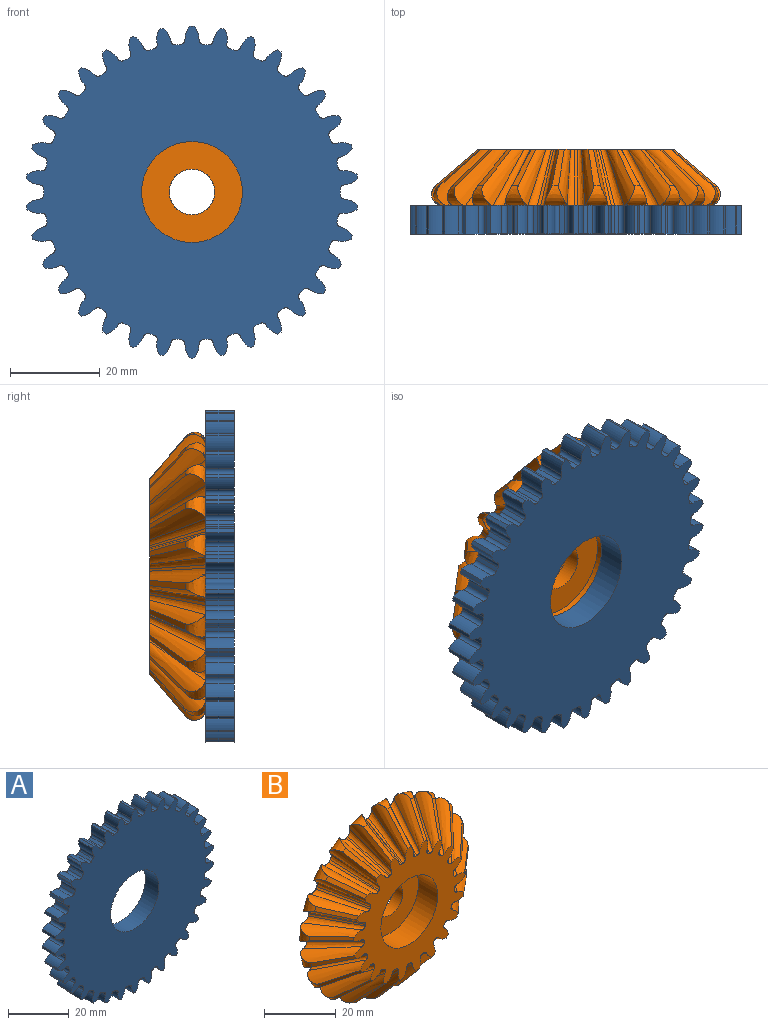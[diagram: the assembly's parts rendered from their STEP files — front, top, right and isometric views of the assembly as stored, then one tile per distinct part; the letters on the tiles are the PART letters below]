
ASSEMBLY  parts=2 mates=1
PART A: 207 faces, bbox 73.8x6.4x74 mm
  f0: cylinder r=33mm len=6.35mm, axis (0,1,0), area 7mm2, adj f34,f35,f40,f204
  f1: cylinder r=33mm len=6.35mm, axis (0,1,0), area 7mm2, adj f34,f35,f199,f205
  f2: cylinder r=33mm len=6.35mm, axis (0,1,0), area 7mm2, adj f34,f35,f194,f200
  f3: cylinder r=33mm len=6.35mm, axis (0,1,0), area 7mm2, adj f34,f35,f189,f195
  f4: cylinder r=33mm len=6.35mm, axis (0,1,0), area 7mm2, adj f34,f35,f184,f190
  f5: cylinder r=33mm len=6.35mm, axis (0,1,0), area 7mm2, adj f34,f35,f179,f185
  f6: cylinder r=33mm len=6.35mm, axis (0,1,0), area 7mm2, adj f34,f35,f174,f180
  f7: cylinder r=33mm len=6.35mm, axis (0,1,0), area 7mm2, adj f34,f35,f169,f175
  f8: cylinder r=33mm len=6.35mm, axis (0,1,0), area 7mm2, adj f34,f35,f164,f170
  f9: cylinder r=33mm len=6.35mm, axis (0,1,0), area 7mm2, adj f34,f35,f159,f165
  f10: cylinder r=33mm len=6.35mm, axis (0,1,0), area 7mm2, adj f34,f35,f154,f160
  f11: cylinder r=33mm len=6.35mm, axis (0,1,0), area 7mm2, adj f34,f35,f149,f155
  f12: cylinder r=33mm len=6.35mm, axis (0,1,0), area 7mm2, adj f34,f35,f144,f150
  f13: cylinder r=33mm len=6.35mm, axis (0,1,0), area 7mm2, adj f34,f35,f139,f145
  f14: cylinder r=33mm len=6.35mm, axis (0,1,0), area 7mm2, adj f34,f35,f134,f140
  f15: cylinder r=33mm len=6.35mm, axis (0,1,0), area 7mm2, adj f34,f35,f129,f135
  f16: cylinder r=33mm len=6.35mm, axis (0,1,0), area 7mm2, adj f34,f35,f124,f130
  f17: cylinder r=33mm len=6.35mm, axis (0,1,0), area 7mm2, adj f34,f35,f119,f125
  f18: cylinder r=33mm len=6.35mm, axis (0,1,0), area 7mm2, adj f34,f35,f114,f120
  f19: cylinder r=33mm len=6.35mm, axis (0,1,0), area 7mm2, adj f34,f35,f109,f115
  f20: cylinder r=33mm len=6.35mm, axis (0,1,0), area 7mm2, adj f34,f35,f104,f110
  f21: cylinder r=33mm len=6.35mm, axis (0,1,0), area 7mm2, adj f34,f35,f99,f105
  f22: cylinder r=33mm len=6.35mm, axis (0,1,0), area 7mm2, adj f34,f35,f94,f100
  f23: cylinder r=33mm len=6.35mm, axis (0,1,0), area 7mm2, adj f34,f35,f89,f95
  f24: cylinder r=33mm len=6.35mm, axis (0,1,0), area 7mm2, adj f34,f35,f84,f90
  f25: cylinder r=33mm len=6.35mm, axis (0,1,0), area 7mm2, adj f34,f35,f79,f85
  f26: cylinder r=33mm len=6.35mm, axis (0,1,0), area 7mm2, adj f34,f35,f74,f80
  f27: cylinder r=33mm len=6.35mm, axis (0,1,0), area 7mm2, adj f34,f35,f69,f75
  f28: cylinder r=33mm len=6.35mm, axis (0,1,0), area 7mm2, adj f34,f35,f64,f70
  f29: cylinder r=33mm len=6.35mm, axis (0,1,0), area 7mm2, adj f34,f35,f59,f65
  f30: cylinder r=33mm len=6.35mm, axis (0,1,0), area 7mm2, adj f34,f35,f54,f60
  f31: cylinder r=33mm len=6.35mm, axis (0,1,0), area 7mm2, adj f34,f35,f49,f55
  f32: cylinder r=33mm len=6.35mm, axis (0,1,0), area 7mm2, adj f34,f35,f44,f50
  f33: cylinder r=33mm len=6.35mm, axis (0,1,0), area 7mm2, adj f34,f35,f39,f45
  f34: plane 74x73.76mm, normal (0,-1,0), area 3393.5mm2, adj f0,f1,f2,f3,f4,f5,f6,f7
  f35: plane 74x73.76mm, normal (0,1,0), area 3393.5mm2, adj f0,f1,f2,f3,f4,f5,f6,f7
  f36: cylinder r=4.53mm len=6.35mm, axis (0,1,0), area 21.2mm2, adj f34,f35,f37,f40
  f37: cylinder r=37mm len=6.35mm, axis (0,1,0), area 5.8mm2, adj f34,f35,f36,f38
  f38: cylinder r=4.53mm len=6.35mm, axis (0,1,0), area 21.2mm2, adj f34,f35,f37,f39
  f39: cylinder r=1mm len=6.35mm, axis (0,1,0), area 9.6mm2, adj f33,f34,f35,f38
  f40: cylinder r=1mm len=6.35mm, axis (0,1,0), area 9.6mm2, adj f0,f34,f35,f36
  f41: cylinder r=4.53mm len=6.35mm, axis (0,1,0), area 21.2mm2, adj f34,f35,f42,f45
  f42: cylinder r=37mm len=6.35mm, axis (0,1,0), area 5.8mm2, adj f34,f35,f41,f43
  f43: cylinder r=4.53mm len=6.35mm, axis (0,1,0), area 21.2mm2, adj f34,f35,f42,f44
  f44: cylinder r=1mm len=6.35mm, axis (0,1,0), area 9.6mm2, adj f32,f34,f35,f43
  f45: cylinder r=1mm len=6.35mm, axis (0,1,0), area 9.6mm2, adj f33,f34,f35,f41
  f46: cylinder r=4.53mm len=6.35mm, axis (0,1,0), area 21.2mm2, adj f34,f35,f47,f50
  f47: cylinder r=37mm len=6.35mm, axis (0,1,0), area 5.8mm2, adj f34,f35,f46,f48
  f48: cylinder r=4.53mm len=6.35mm, axis (0,1,0), area 21.2mm2, adj f34,f35,f47,f49
  f49: cylinder r=1mm len=6.35mm, axis (0,1,0), area 9.6mm2, adj f31,f34,f35,f48
  f50: cylinder r=1mm len=6.35mm, axis (0,1,0), area 9.6mm2, adj f32,f34,f35,f46
  f51: cylinder r=4.53mm len=6.35mm, axis (0,1,0), area 21.2mm2, adj f34,f35,f52,f55
  f52: cylinder r=37mm len=6.35mm, axis (0,1,0), area 5.8mm2, adj f34,f35,f51,f53
  f53: cylinder r=4.53mm len=6.35mm, axis (0,1,0), area 21.2mm2, adj f34,f35,f52,f54
  f54: cylinder r=1mm len=6.35mm, axis (0,1,0), area 9.6mm2, adj f30,f34,f35,f53
  f55: cylinder r=1mm len=6.35mm, axis (0,1,0), area 9.6mm2, adj f31,f34,f35,f51
  f56: cylinder r=4.53mm len=6.35mm, axis (0,1,0), area 21.2mm2, adj f34,f35,f57,f60
  f57: cylinder r=37mm len=6.35mm, axis (0,1,0), area 5.8mm2, adj f34,f35,f56,f58
  f58: cylinder r=4.53mm len=6.35mm, axis (0,1,0), area 21.2mm2, adj f34,f35,f57,f59
  f59: cylinder r=1mm len=6.35mm, axis (0,1,0), area 9.6mm2, adj f29,f34,f35,f58
  f60: cylinder r=1mm len=6.35mm, axis (0,1,0), area 9.6mm2, adj f30,f34,f35,f56
  f61: cylinder r=4.53mm len=6.35mm, axis (0,1,0), area 21.2mm2, adj f34,f35,f62,f65
  f62: cylinder r=37mm len=6.35mm, axis (0,1,0), area 5.8mm2, adj f34,f35,f61,f63
  f63: cylinder r=4.53mm len=6.35mm, axis (0,1,0), area 21.2mm2, adj f34,f35,f62,f64
  f64: cylinder r=1mm len=6.35mm, axis (0,1,0), area 9.6mm2, adj f28,f34,f35,f63
  f65: cylinder r=1mm len=6.35mm, axis (0,1,0), area 9.6mm2, adj f29,f34,f35,f61
  f66: cylinder r=4.53mm len=6.35mm, axis (0,1,0), area 21.2mm2, adj f34,f35,f67,f70
  f67: cylinder r=37mm len=6.35mm, axis (0,1,0), area 5.8mm2, adj f34,f35,f66,f68
  f68: cylinder r=4.53mm len=6.35mm, axis (0,1,0), area 21.2mm2, adj f34,f35,f67,f69
  f69: cylinder r=1mm len=6.35mm, axis (0,1,0), area 9.6mm2, adj f27,f34,f35,f68
  f70: cylinder r=1mm len=6.35mm, axis (0,1,0), area 9.6mm2, adj f28,f34,f35,f66
  f71: cylinder r=4.53mm len=6.35mm, axis (0,1,0), area 21.2mm2, adj f34,f35,f72,f75
  f72: cylinder r=37mm len=6.35mm, axis (0,1,0), area 5.8mm2, adj f34,f35,f71,f73
  f73: cylinder r=4.53mm len=6.35mm, axis (0,1,0), area 21.2mm2, adj f34,f35,f72,f74
  f74: cylinder r=1mm len=6.35mm, axis (0,1,0), area 9.6mm2, adj f26,f34,f35,f73
  f75: cylinder r=1mm len=6.35mm, axis (0,1,0), area 9.6mm2, adj f27,f34,f35,f71
  f76: cylinder r=4.53mm len=6.35mm, axis (0,1,0), area 21.2mm2, adj f34,f35,f77,f80
  f77: cylinder r=37mm len=6.35mm, axis (0,1,0), area 5.8mm2, adj f34,f35,f76,f78
  f78: cylinder r=4.53mm len=6.35mm, axis (0,1,0), area 21.2mm2, adj f34,f35,f77,f79
  f79: cylinder r=1mm len=6.35mm, axis (0,1,0), area 9.6mm2, adj f25,f34,f35,f78
  f80: cylinder r=1mm len=6.35mm, axis (0,1,0), area 9.6mm2, adj f26,f34,f35,f76
  f81: cylinder r=4.53mm len=6.35mm, axis (0,1,0), area 21.2mm2, adj f34,f35,f82,f85
  f82: cylinder r=37mm len=6.35mm, axis (0,1,0), area 5.8mm2, adj f34,f35,f81,f83
  f83: cylinder r=4.53mm len=6.35mm, axis (0,1,0), area 21.2mm2, adj f34,f35,f82,f84
  f84: cylinder r=1mm len=6.35mm, axis (0,1,0), area 9.6mm2, adj f24,f34,f35,f83
  f85: cylinder r=1mm len=6.35mm, axis (0,1,0), area 9.6mm2, adj f25,f34,f35,f81
  f86: cylinder r=4.53mm len=6.35mm, axis (0,1,0), area 21.2mm2, adj f34,f35,f87,f90
  f87: cylinder r=37mm len=6.35mm, axis (0,1,0), area 5.8mm2, adj f34,f35,f86,f88
  f88: cylinder r=4.53mm len=6.35mm, axis (0,1,0), area 21.2mm2, adj f34,f35,f87,f89
  f89: cylinder r=1mm len=6.35mm, axis (0,1,0), area 9.6mm2, adj f23,f34,f35,f88
  f90: cylinder r=1mm len=6.35mm, axis (0,1,0), area 9.6mm2, adj f24,f34,f35,f86
  f91: cylinder r=4.53mm len=6.35mm, axis (0,1,0), area 21.2mm2, adj f34,f35,f92,f95
  f92: cylinder r=37mm len=6.35mm, axis (0,1,0), area 5.8mm2, adj f34,f35,f91,f93
  f93: cylinder r=4.53mm len=6.35mm, axis (0,1,0), area 21.2mm2, adj f34,f35,f92,f94
  f94: cylinder r=1mm len=6.35mm, axis (0,1,0), area 9.6mm2, adj f22,f34,f35,f93
  f95: cylinder r=1mm len=6.35mm, axis (0,1,0), area 9.6mm2, adj f23,f34,f35,f91
  f96: cylinder r=4.53mm len=6.35mm, axis (0,1,0), area 21.2mm2, adj f34,f35,f97,f100
  f97: cylinder r=37mm len=6.35mm, axis (0,1,0), area 5.8mm2, adj f34,f35,f96,f98
  f98: cylinder r=4.53mm len=6.35mm, axis (0,1,0), area 21.2mm2, adj f34,f35,f97,f99
  f99: cylinder r=1mm len=6.35mm, axis (0,1,0), area 9.6mm2, adj f21,f34,f35,f98
  f100: cylinder r=1mm len=6.35mm, axis (0,1,0), area 9.6mm2, adj f22,f34,f35,f96
  f101: cylinder r=4.53mm len=6.35mm, axis (0,1,0), area 21.2mm2, adj f34,f35,f102,f105
  f102: cylinder r=37mm len=6.35mm, axis (0,1,0), area 5.8mm2, adj f34,f35,f101,f103
  f103: cylinder r=4.53mm len=6.35mm, axis (0,1,0), area 21.2mm2, adj f34,f35,f102,f104
  f104: cylinder r=1mm len=6.35mm, axis (0,1,0), area 9.6mm2, adj f20,f34,f35,f103
  f105: cylinder r=1mm len=6.35mm, axis (0,1,0), area 9.6mm2, adj f21,f34,f35,f101
  f106: cylinder r=4.53mm len=6.35mm, axis (0,1,0), area 21.2mm2, adj f34,f35,f107,f110
  f107: cylinder r=37mm len=6.35mm, axis (0,1,0), area 5.8mm2, adj f34,f35,f106,f108
  f108: cylinder r=4.53mm len=6.35mm, axis (0,1,0), area 21.2mm2, adj f34,f35,f107,f109
  f109: cylinder r=1mm len=6.35mm, axis (0,1,0), area 9.6mm2, adj f19,f34,f35,f108
  f110: cylinder r=1mm len=6.35mm, axis (0,1,0), area 9.6mm2, adj f20,f34,f35,f106
  f111: cylinder r=4.53mm len=6.35mm, axis (0,1,0), area 21.2mm2, adj f34,f35,f112,f115
  f112: cylinder r=37mm len=6.35mm, axis (0,1,0), area 5.8mm2, adj f34,f35,f111,f113
  f113: cylinder r=4.53mm len=6.35mm, axis (0,1,0), area 21.2mm2, adj f34,f35,f112,f114
  f114: cylinder r=1mm len=6.35mm, axis (0,1,0), area 9.6mm2, adj f18,f34,f35,f113
  f115: cylinder r=1mm len=6.35mm, axis (0,1,0), area 9.6mm2, adj f19,f34,f35,f111
  f116: cylinder r=4.53mm len=6.35mm, axis (0,1,0), area 21.2mm2, adj f34,f35,f117,f120
  f117: cylinder r=37mm len=6.35mm, axis (0,1,0), area 5.8mm2, adj f34,f35,f116,f118
  f118: cylinder r=4.53mm len=6.35mm, axis (0,1,0), area 21.2mm2, adj f34,f35,f117,f119
  f119: cylinder r=1mm len=6.35mm, axis (0,1,0), area 9.6mm2, adj f17,f34,f35,f118
  f120: cylinder r=1mm len=6.35mm, axis (0,1,0), area 9.6mm2, adj f18,f34,f35,f116
  f121: cylinder r=4.53mm len=6.35mm, axis (0,1,0), area 21.2mm2, adj f34,f35,f122,f125
  f122: cylinder r=37mm len=6.35mm, axis (0,1,0), area 5.8mm2, adj f34,f35,f121,f123
  f123: cylinder r=4.53mm len=6.35mm, axis (0,1,0), area 21.2mm2, adj f34,f35,f122,f124
  f124: cylinder r=1mm len=6.35mm, axis (0,1,0), area 9.6mm2, adj f16,f34,f35,f123
  f125: cylinder r=1mm len=6.35mm, axis (0,1,0), area 9.6mm2, adj f17,f34,f35,f121
  f126: cylinder r=4.53mm len=6.35mm, axis (0,1,0), area 21.2mm2, adj f34,f35,f127,f130
  f127: cylinder r=37mm len=6.35mm, axis (0,1,0), area 5.8mm2, adj f34,f35,f126,f128
  f128: cylinder r=4.53mm len=6.35mm, axis (0,1,0), area 21.2mm2, adj f34,f35,f127,f129
  f129: cylinder r=1mm len=6.35mm, axis (0,1,0), area 9.6mm2, adj f15,f34,f35,f128
  f130: cylinder r=1mm len=6.35mm, axis (0,1,0), area 9.6mm2, adj f16,f34,f35,f126
  f131: cylinder r=4.53mm len=6.35mm, axis (0,1,0), area 21.2mm2, adj f34,f35,f132,f135
  f132: cylinder r=37mm len=6.35mm, axis (0,1,0), area 5.8mm2, adj f34,f35,f131,f133
  f133: cylinder r=4.53mm len=6.35mm, axis (0,1,0), area 21.2mm2, adj f34,f35,f132,f134
  f134: cylinder r=1mm len=6.35mm, axis (0,1,0), area 9.6mm2, adj f14,f34,f35,f133
  f135: cylinder r=1mm len=6.35mm, axis (0,1,0), area 9.6mm2, adj f15,f34,f35,f131
  f136: cylinder r=4.53mm len=6.35mm, axis (0,1,0), area 21.2mm2, adj f34,f35,f137,f140
  f137: cylinder r=37mm len=6.35mm, axis (0,1,0), area 5.8mm2, adj f34,f35,f136,f138
  f138: cylinder r=4.53mm len=6.35mm, axis (0,1,0), area 21.2mm2, adj f34,f35,f137,f139
  f139: cylinder r=1mm len=6.35mm, axis (0,1,0), area 9.6mm2, adj f13,f34,f35,f138
  f140: cylinder r=1mm len=6.35mm, axis (0,1,0), area 9.6mm2, adj f14,f34,f35,f136
  f141: cylinder r=4.53mm len=6.35mm, axis (0,1,0), area 21.2mm2, adj f34,f35,f142,f145
  f142: cylinder r=37mm len=6.35mm, axis (0,1,0), area 5.8mm2, adj f34,f35,f141,f143
  f143: cylinder r=4.53mm len=6.35mm, axis (0,1,0), area 21.2mm2, adj f34,f35,f142,f144
  f144: cylinder r=1mm len=6.35mm, axis (0,1,0), area 9.6mm2, adj f12,f34,f35,f143
  f145: cylinder r=1mm len=6.35mm, axis (0,1,0), area 9.6mm2, adj f13,f34,f35,f141
  f146: cylinder r=4.53mm len=6.35mm, axis (0,1,0), area 21.2mm2, adj f34,f35,f147,f150
  f147: cylinder r=37mm len=6.35mm, axis (0,1,0), area 5.8mm2, adj f34,f35,f146,f148
  f148: cylinder r=4.53mm len=6.35mm, axis (0,1,0), area 21.2mm2, adj f34,f35,f147,f149
  f149: cylinder r=1mm len=6.35mm, axis (0,1,0), area 9.6mm2, adj f11,f34,f35,f148
  f150: cylinder r=1mm len=6.35mm, axis (0,1,0), area 9.6mm2, adj f12,f34,f35,f146
  f151: cylinder r=4.53mm len=6.35mm, axis (0,1,0), area 21.2mm2, adj f34,f35,f152,f155
  f152: cylinder r=37mm len=6.35mm, axis (0,1,0), area 5.8mm2, adj f34,f35,f151,f153
  f153: cylinder r=4.53mm len=6.35mm, axis (0,1,0), area 21.2mm2, adj f34,f35,f152,f154
  f154: cylinder r=1mm len=6.35mm, axis (0,1,0), area 9.6mm2, adj f10,f34,f35,f153
  f155: cylinder r=1mm len=6.35mm, axis (0,1,0), area 9.6mm2, adj f11,f34,f35,f151
  f156: cylinder r=4.53mm len=6.35mm, axis (0,1,0), area 21.2mm2, adj f34,f35,f157,f160
  f157: cylinder r=37mm len=6.35mm, axis (0,1,0), area 5.8mm2, adj f34,f35,f156,f158
  f158: cylinder r=4.53mm len=6.35mm, axis (0,1,0), area 21.2mm2, adj f34,f35,f157,f159
  f159: cylinder r=1mm len=6.35mm, axis (0,1,0), area 9.6mm2, adj f9,f34,f35,f158
  f160: cylinder r=1mm len=6.35mm, axis (0,1,0), area 9.6mm2, adj f10,f34,f35,f156
  f161: cylinder r=4.53mm len=6.35mm, axis (0,1,0), area 21.2mm2, adj f34,f35,f162,f165
  f162: cylinder r=37mm len=6.35mm, axis (0,1,0), area 5.8mm2, adj f34,f35,f161,f163
  f163: cylinder r=4.53mm len=6.35mm, axis (0,1,0), area 21.2mm2, adj f34,f35,f162,f164
  f164: cylinder r=1mm len=6.35mm, axis (0,1,0), area 9.6mm2, adj f8,f34,f35,f163
  f165: cylinder r=1mm len=6.35mm, axis (0,1,0), area 9.6mm2, adj f9,f34,f35,f161
  f166: cylinder r=4.53mm len=6.35mm, axis (0,1,0), area 21.2mm2, adj f34,f35,f167,f170
  f167: cylinder r=37mm len=6.35mm, axis (0,1,0), area 5.8mm2, adj f34,f35,f166,f168
  f168: cylinder r=4.53mm len=6.35mm, axis (0,1,0), area 21.2mm2, adj f34,f35,f167,f169
  f169: cylinder r=1mm len=6.35mm, axis (0,1,0), area 9.6mm2, adj f7,f34,f35,f168
  f170: cylinder r=1mm len=6.35mm, axis (0,1,0), area 9.6mm2, adj f8,f34,f35,f166
  f171: cylinder r=4.53mm len=6.35mm, axis (0,1,0), area 21.2mm2, adj f34,f35,f172,f175
  f172: cylinder r=37mm len=6.35mm, axis (0,1,0), area 5.8mm2, adj f34,f35,f171,f173
  f173: cylinder r=4.53mm len=6.35mm, axis (0,1,0), area 21.2mm2, adj f34,f35,f172,f174
  f174: cylinder r=1mm len=6.35mm, axis (0,1,0), area 9.6mm2, adj f6,f34,f35,f173
  f175: cylinder r=1mm len=6.35mm, axis (0,1,0), area 9.6mm2, adj f7,f34,f35,f171
  f176: cylinder r=4.53mm len=6.35mm, axis (0,1,0), area 21.2mm2, adj f34,f35,f177,f180
  f177: cylinder r=37mm len=6.35mm, axis (0,1,0), area 5.8mm2, adj f34,f35,f176,f178
  f178: cylinder r=4.53mm len=6.35mm, axis (0,1,0), area 21.2mm2, adj f34,f35,f177,f179
  f179: cylinder r=1mm len=6.35mm, axis (0,1,0), area 9.6mm2, adj f5,f34,f35,f178
  f180: cylinder r=1mm len=6.35mm, axis (0,1,0), area 9.6mm2, adj f6,f34,f35,f176
  f181: cylinder r=4.53mm len=6.35mm, axis (0,1,0), area 21.2mm2, adj f34,f35,f182,f185
  f182: cylinder r=37mm len=6.35mm, axis (0,1,0), area 5.8mm2, adj f34,f35,f181,f183
  f183: cylinder r=4.53mm len=6.35mm, axis (0,1,0), area 21.2mm2, adj f34,f35,f182,f184
  f184: cylinder r=1mm len=6.35mm, axis (0,1,0), area 9.6mm2, adj f4,f34,f35,f183
  f185: cylinder r=1mm len=6.35mm, axis (0,1,0), area 9.6mm2, adj f5,f34,f35,f181
  f186: cylinder r=4.53mm len=6.35mm, axis (0,1,0), area 21.2mm2, adj f34,f35,f187,f190
  f187: cylinder r=37mm len=6.35mm, axis (0,1,0), area 5.8mm2, adj f34,f35,f186,f188
  f188: cylinder r=4.53mm len=6.35mm, axis (0,1,0), area 21.2mm2, adj f34,f35,f187,f189
  f189: cylinder r=1mm len=6.35mm, axis (0,1,0), area 9.6mm2, adj f3,f34,f35,f188
  f190: cylinder r=1mm len=6.35mm, axis (0,1,0), area 9.6mm2, adj f4,f34,f35,f186
  f191: cylinder r=4.53mm len=6.35mm, axis (0,1,0), area 21.2mm2, adj f34,f35,f192,f195
  f192: cylinder r=37mm len=6.35mm, axis (0,1,0), area 5.8mm2, adj f34,f35,f191,f193
  f193: cylinder r=4.53mm len=6.35mm, axis (0,1,0), area 21.2mm2, adj f34,f35,f192,f194
  f194: cylinder r=1mm len=6.35mm, axis (0,1,0), area 9.6mm2, adj f2,f34,f35,f193
  f195: cylinder r=1mm len=6.35mm, axis (0,1,0), area 9.6mm2, adj f3,f34,f35,f191
  f196: cylinder r=4.53mm len=6.35mm, axis (0,1,0), area 21.2mm2, adj f34,f35,f197,f200
  f197: cylinder r=37mm len=6.35mm, axis (0,1,0), area 5.8mm2, adj f34,f35,f196,f198
  f198: cylinder r=4.53mm len=6.35mm, axis (0,1,0), area 21.2mm2, adj f34,f35,f197,f199
  f199: cylinder r=1mm len=6.35mm, axis (0,1,0), area 9.6mm2, adj f1,f34,f35,f198
  f200: cylinder r=1mm len=6.35mm, axis (0,1,0), area 9.6mm2, adj f2,f34,f35,f196
  f201: cylinder r=4.53mm len=6.35mm, axis (0,1,0), area 21.2mm2, adj f34,f35,f202,f205
  f202: cylinder r=37mm len=6.35mm, axis (0,1,0), area 5.8mm2, adj f34,f35,f201,f203
  f203: cylinder r=4.53mm len=6.35mm, axis (0,1,0), area 21.2mm2, adj f34,f35,f202,f204
  f204: cylinder r=1mm len=6.35mm, axis (0,1,0), area 9.6mm2, adj f0,f34,f35,f203
  f205: cylinder r=1mm len=6.35mm, axis (0,1,0), area 9.6mm2, adj f1,f34,f35,f201
  f206: cylinder r=11.24mm len=22.48mm, axis (0,-1,0), area 448.4mm2, adj f34,f35
PART B: 154 faces, bbox 73.2x12.7x73.2 mm
  f0: cylinder r=5.08mm len=10.16mm, axis (0,-1,0), area 115.1mm2, adj f150,f152
  f1: cone r=17.69mm half-angle=39.1deg, axis (0,1,0), area 10.1mm2, adj f2,f8,f10,f145
  f2: bspline ~12.65x12.36mm, area 30.4mm2, adj f1,f7,f8,f9,f10
  f3: cone r=17.69mm half-angle=39.1deg, axis (0,1,0), area 10.1mm2, adj f4,f8,f10,f11
  f4: bspline ~12.65x12.36mm, area 30mm2, adj f3,f5,f8,f9,f10
  f5: bspline ~17.78x12.48mm, area 52.6mm2, adj f4,f6,f9,f10
  f6: bspline ~14.81x12.65mm, area 16.8mm2, adj f5,f7,f9,f10
  f7: bspline ~17.77x12.48mm, area 53mm2, adj f2,f6,f9,f10
  f8: plane 59.4x59.29mm, normal (0,1,0), area 2258.6mm2, adj f1,f2,f3,f4,f9,f11,f12,f13
  f9: bspline ~6.99x6.97mm, area 22.1mm2, adj f2,f4,f5,f6,f7,f8
  f10: plane 43.78x43.68mm, normal (0,-1,0), area 841.2mm2, adj f1,f2,f3,f4,f5,f6,f7,f11
  f11: bspline ~12.65x11.85mm, area 30.4mm2, adj f3,f8,f10,f16,f17
  f12: cone r=17.69mm half-angle=39.1deg, axis (0,1,0), area 10.1mm2, adj f8,f10,f13,f18
  f13: bspline ~12.5x11.67mm, area 30mm2, adj f8,f10,f12,f14,f17
  f14: bspline ~17.34x12.65mm, area 52.6mm2, adj f10,f13,f15,f17
  f15: bspline ~9.39x8.03mm, area 16.8mm2, adj f10,f14,f16,f17
  f16: bspline ~16.94x12.65mm, area 53mm2, adj f10,f11,f15,f17
  f17: bspline ~8.6x8.53mm, area 22.1mm2, adj f8,f11,f13,f14,f15,f16
  f18: bspline ~12.65x10.36mm, area 30.4mm2, adj f8,f10,f12,f23,f24
  f19: cone r=17.69mm half-angle=39.1deg, axis (0,1,0), area 10.1mm2, adj f8,f10,f20,f25
  f20: bspline ~12.5x10.08mm, area 30mm2, adj f8,f10,f19,f21,f24
  f21: bspline ~15.21x12.65mm, area 52.6mm2, adj f10,f20,f22,f24
  f22: bspline ~8.55x8.03mm, area 16.8mm2, adj f10,f21,f23,f24
  f23: bspline ~14.31x12.48mm, area 53mm2, adj f10,f18,f22,f24
  f24: bspline ~9.54x9.5mm, area 22.1mm2, adj f8,f18,f20,f21,f22,f23
  f25: bspline ~12.5x9.53mm, area 30.4mm2, adj f8,f10,f19,f30,f31
  f26: cone r=17.69mm half-angle=39.1deg, axis (0,1,0), area 10.1mm2, adj f8,f10,f27,f32
  f27: bspline ~12.65x9.83mm, area 30mm2, adj f8,f10,f26,f28,f31
  f28: bspline ~13.59x12.65mm, area 52.6mm2, adj f10,f27,f29,f31
  f29: bspline ~12.65x12.44mm, area 16.8mm2, adj f10,f28,f30,f31
  f30: bspline ~14.42x12.65mm, area 53mm2, adj f10,f25,f29,f31
  f31: bspline ~9.62x9.62mm, area 22.1mm2, adj f8,f25,f27,f28,f29,f30
  f32: bspline ~12.65x11.48mm, area 30.4mm2, adj f8,f10,f26,f37,f38
  f33: cone r=17.69mm half-angle=39.1deg, axis (0,1,0), area 10.1mm2, adj f8,f10,f34,f39
  f34: bspline ~12.5x11.42mm, area 30mm2, adj f8,f10,f33,f35,f38
  f35: bspline ~16.44x12.65mm, area 52.6mm2, adj f10,f34,f36,f38
  f36: bspline ~14.28x12.65mm, area 16.8mm2, adj f10,f35,f37,f38
  f37: bspline ~16.92x12.65mm, area 53mm2, adj f10,f32,f36,f38
  f38: bspline ~8.88x8.86mm, area 22.1mm2, adj f8,f32,f34,f35,f36,f37
  f39: bspline ~12.5x12.19mm, area 30.4mm2, adj f8,f10,f33,f44,f45
  f40: cone r=17.69mm half-angle=39.1deg, axis (0,1,0), area 10.1mm2, adj f8,f10,f41,f46
  f41: bspline ~12.5x12.2mm, area 30mm2, adj f8,f10,f40,f42,f45
  f42: bspline ~17.83x12.65mm, area 52.6mm2, adj f10,f41,f43,f45
  f43: bspline ~14.86x12.65mm, area 16.8mm2, adj f10,f42,f44,f45
  f44: bspline ~17.92x12.65mm, area 53mm2, adj f10,f39,f43,f45
  f45: bspline ~7.36x7.3mm, area 22.1mm2, adj f8,f39,f41,f42,f43,f44
  f46: bspline ~12.65x12.07mm, area 30.4mm2, adj f8,f10,f40,f51,f52
  f47: cone r=17.69mm half-angle=39.1deg, axis (0,1,0), area 10.1mm2, adj f8,f10,f48,f53
  f48: bspline ~12.5x11.91mm, area 30mm2, adj f8,f10,f47,f49,f52
  f49: bspline ~17.64x12.65mm, area 52.6mm2, adj f10,f48,f50,f52
  f50: bspline ~9.47x8.03mm, area 16.8mm2, adj f10,f49,f51,f52
  f51: bspline ~17.18x12.48mm, area 53mm2, adj f10,f46,f50,f52
  f52: bspline ~8.24x8.17mm, area 22.1mm2, adj f8,f46,f48,f49,f50,f51
  f53: bspline ~12.65x10.81mm, area 30.4mm2, adj f8,f10,f47,f58,f59
  f54: cone r=17.69mm half-angle=39.1deg, axis (0,1,0), area 10.1mm2, adj f8,f10,f55,f60
  f55: bspline ~12.65x10.66mm, area 30mm2, adj f8,f10,f54,f56,f59
  f56: bspline ~15.88x12.65mm, area 52.6mm2, adj f10,f55,f57,f59
  f57: bspline ~13.58x12.65mm, area 16.8mm2, adj f10,f56,f58,f59
  f58: bspline ~15.2x12.65mm, area 53mm2, adj f10,f53,f57,f59
  f59: bspline ~9.38x9.33mm, area 22.1mm2, adj f8,f53,f55,f56,f57,f58
  f60: bspline ~12.65x9.01mm, area 30.4mm2, adj f8,f10,f54,f65,f66
  f61: cone r=17.69mm half-angle=39.1deg, axis (0,1,0), area 10.1mm2, adj f8,f10,f62,f67
  f62: bspline ~12.65x9.27mm, area 30mm2, adj f8,f10,f61,f63,f66
  f63: bspline ~12.61x12.55mm, area 52.6mm2, adj f10,f62,f64,f66
  f64: bspline ~12.65x11.8mm, area 16.8mm2, adj f10,f63,f65,f66
  f65: bspline ~13.48x12.48mm, area 53mm2, adj f10,f60,f64,f66
  f66: bspline ~9.68x9.67mm, area 22.1mm2, adj f8,f60,f62,f63,f64,f65
  f67: bspline ~12.5x11mm, area 30.4mm2, adj f8,f10,f61,f72,f73
  f68: cone r=17.69mm half-angle=39.1deg, axis (0,1,0), area 10.1mm2, adj f8,f10,f69,f74
  f69: bspline ~12.5x11.08mm, area 30mm2, adj f8,f10,f68,f70,f73
  f70: bspline ~15.71x12.48mm, area 52.6mm2, adj f10,f69,f71,f73
  f71: bspline ~13.94x12.65mm, area 16.8mm2, adj f10,f70,f72,f73
  f72: bspline ~16.43x12.65mm, area 53mm2, adj f10,f67,f71,f73
  f73: bspline ~9.15x9.13mm, area 22.1mm2, adj f8,f67,f69,f70,f71,f72
  f74: bspline ~12.5x12.09mm, area 30.4mm2, adj f8,f10,f68,f79,f80
  f75: cone r=17.69mm half-angle=39.1deg, axis (0,1,0), area 10.1mm2, adj f8,f10,f76,f81
  f76: bspline ~12.5x12.1mm, area 30mm2, adj f8,f10,f75,f77,f80
  f77: bspline ~17.63x12.65mm, area 52.6mm2, adj f10,f76,f78,f80
  f78: bspline ~9.48x8.03mm, area 16.8mm2, adj f10,f77,f79,f80
  f79: bspline ~17.82x12.65mm, area 53mm2, adj f10,f74,f78,f80
  f80: bspline ~7.81x7.76mm, area 22.1mm2, adj f8,f74,f76,f77,f78,f79
  f81: bspline ~12.5x12.1mm, area 30.4mm2, adj f8,f10,f75,f86,f87
  f82: cone r=17.69mm half-angle=39.1deg, axis (0,1,0), area 10.1mm2, adj f8,f10,f83,f88
  f83: bspline ~12.5x12.09mm, area 30mm2, adj f8,f10,f82,f84,f87
  f84: bspline ~17.83x12.65mm, area 52.6mm2, adj f10,f83,f85,f87
  f85: bspline ~9.49x8.03mm, area 16.8mm2, adj f10,f84,f86,f87
  f86: bspline ~17.63x12.65mm, area 53mm2, adj f10,f81,f85,f87
  f87: bspline ~7.84x7.76mm, area 22.1mm2, adj f8,f81,f83,f84,f85,f86
  f88: bspline ~12.5x11.09mm, area 30.4mm2, adj f8,f10,f82,f93,f94
  f89: cone r=17.69mm half-angle=39.1deg, axis (0,1,0), area 10.1mm2, adj f8,f10,f90,f95
  f90: bspline ~12.65x11.1mm, area 30mm2, adj f8,f10,f89,f91,f94
  f91: bspline ~16.32x12.48mm, area 52.6mm2, adj f10,f90,f92,f94
  f92: bspline ~14x12.65mm, area 16.8mm2, adj f10,f91,f93,f94
  f93: bspline ~15.87x12.65mm, area 53mm2, adj f10,f88,f92,f94
  f94: bspline ~9.17x9.12mm, area 22.1mm2, adj f8,f88,f90,f91,f92,f93
  f95: bspline ~12.5x9.18mm, area 30.4mm2, adj f8,f10,f89,f100,f101
  f96: cone r=17.69mm half-angle=39.1deg, axis (0,1,0), area 10.1mm2, adj f8,f10,f97,f102
  f97: bspline ~12.5x8.93mm, area 30mm2, adj f8,f10,f96,f98,f101
  f98: bspline ~13.62x12.65mm, area 52.6mm2, adj f10,f97,f99,f101
  f99: bspline ~12.65x11.89mm, area 16.8mm2, adj f10,f98,f100,f101
  f100: bspline ~12.58x12.57mm, area 53mm2, adj f10,f95,f99,f101
  f101: bspline ~9.69x9.66mm, area 22.1mm2, adj f8,f95,f97,f98,f99,f100
  f102: bspline ~12.5x10.57mm, area 30.4mm2, adj f8,f10,f96,f107,f108
  f103: cone r=17.69mm half-angle=39.1deg, axis (0,1,0), area 10.1mm2, adj f8,f10,f104,f109
  f104: bspline ~12.5x10.68mm, area 30mm2, adj f8,f10,f103,f105,f108
  f105: bspline ~15.18x12.65mm, area 52.6mm2, adj f10,f104,f106,f108
  f106: bspline ~13.51x12.65mm, area 16.8mm2, adj f10,f105,f107,f108
  f107: bspline ~15.85x12.65mm, area 53mm2, adj f10,f102,f106,f108
  f108: bspline ~9.36x9.35mm, area 22.1mm2, adj f8,f102,f104,f105,f106,f107
  f109: bspline ~12.5x11.91mm, area 30.4mm2, adj f8,f10,f103,f114,f115
  f110: cone r=17.69mm half-angle=39.1deg, axis (0,1,0), area 10.1mm2, adj f8,f10,f111,f116
  f111: bspline ~12.65x12.07mm, area 30mm2, adj f8,f10,f110,f112,f115
  f112: bspline ~17.33x12.65mm, area 52.6mm2, adj f10,f111,f113,f115
  f113: bspline ~14.74x12.65mm, area 16.8mm2, adj f10,f112,f114,f115
  f114: bspline ~17.62x12.65mm, area 53mm2, adj f10,f109,f113,f115
  f115: bspline ~8.21x8.17mm, area 22.1mm2, adj f8,f109,f111,f112,f113,f114
  f116: bspline ~12.65x12.33mm, area 30.4mm2, adj f8,f10,f110,f121,f122
  f117: cone r=17.69mm half-angle=39.1deg, axis (0,1,0), area 10.1mm2, adj f8,f10,f118,f123
  f118: bspline ~12.5x12.19mm, area 30mm2, adj f8,f10,f117,f119,f122
  f119: bspline ~17.93x12.65mm, area 52.6mm2, adj f10,f118,f120,f122
  f120: bspline ~9.47x8.03mm, area 16.8mm2, adj f10,f119,f121,f122
  f121: bspline ~17.83x12.65mm, area 53mm2, adj f10,f116,f120,f122
  f122: bspline ~7.39x7.3mm, area 22.1mm2, adj f8,f116,f118,f119,f120,f121
  f123: bspline ~12.5x11.43mm, area 30.4mm2, adj f8,f10,f117,f128,f129
  f124: cone r=17.69mm half-angle=39.1deg, axis (0,1,0), area 10.1mm2, adj f8,f10,f125,f130
  f125: bspline ~12.65x11.48mm, area 30mm2, adj f8,f10,f124,f126,f129
  f126: bspline ~16.94x12.65mm, area 52.6mm2, adj f10,f125,f127,f129
  f127: bspline ~9.25x8.03mm, area 16.8mm2, adj f10,f126,f128,f129
  f128: bspline ~16.45x12.65mm, area 53mm2, adj f10,f123,f127,f129
  f129: bspline ~8.91x8.85mm, area 22.1mm2, adj f8,f123,f125,f126,f127,f128
  f130: bspline ~12.65x9.85mm, area 30.4mm2, adj f8,f10,f124,f135,f136
  f131: cone r=17.69mm half-angle=39.1deg, axis (0,1,0), area 10.1mm2, adj f8,f10,f132,f137
  f132: bspline ~12.5x9.53mm, area 30mm2, adj f8,f10,f131,f133,f136
  f133: bspline ~14.45x12.65mm, area 52.6mm2, adj f10,f132,f134,f136
  f134: bspline ~8.21x8.03mm, area 16.8mm2, adj f10,f133,f135,f136
  f135: bspline ~13.48x12.48mm, area 53mm2, adj f10,f130,f134,f136
  f136: bspline ~9.64x9.61mm, area 22.1mm2, adj f8,f130,f132,f133,f134,f135
  f137: bspline ~12.5x10.08mm, area 30.4mm2, adj f8,f10,f131,f142,f143
  f138: cone r=17.69mm half-angle=39.1deg, axis (0,1,0), area 10.1mm2, adj f8,f10,f139,f144
  f139: bspline ~12.65x10.34mm, area 30mm2, adj f8,f10,f138,f140,f143
  f140: bspline ~14.29x12.48mm, area 52.6mm2, adj f10,f139,f141,f143
  f141: bspline ~8.5x8.03mm, area 16.8mm2, adj f10,f140,f142,f143
  f142: bspline ~15.18x12.65mm, area 53mm2, adj f10,f137,f141,f143
  f143: bspline ~9.51x9.51mm, area 22.1mm2, adj f8,f137,f139,f140,f141,f142
  f144: bspline ~12.5x11.67mm, area 30.4mm2, adj f8,f10,f138,f148,f149
  f145: bspline ~12.65x11.84mm, area 30mm2, adj f1,f8,f10,f146,f149
  f146: bspline ~16.93x12.65mm, area 52.6mm2, adj f10,f145,f147,f149
  f147: bspline ~9.36x8.03mm, area 16.8mm2, adj f10,f146,f148,f149
  f148: bspline ~17.32x12.65mm, area 53mm2, adj f10,f144,f147,f149
  f149: bspline ~8.57x8.54mm, area 22.1mm2, adj f8,f144,f145,f146,f147,f148
  f150: plane 22.48x22.48mm, normal (0,-1,0), area 315.8mm2, adj f0,f151
  f151: cylinder r=11.24mm len=22.48mm, axis (0,-1,0), area 538.1mm2, adj f10,f150
  f152: plane 22.48x22.48mm, normal (0,1,0), area 315.8mm2, adj f0,f153
  f153: cylinder r=11.24mm len=22.48mm, axis (0,1,0), area 89.7mm2, adj f8,f152
PLACE A at identity fixed
PLACE B rot(axis=(1,0,0),180deg) t=(0,15.88,0)mm
MATE fastened A.f0 <-> B.f26  axis (0,1,0) through (0,3.18,0)mm
